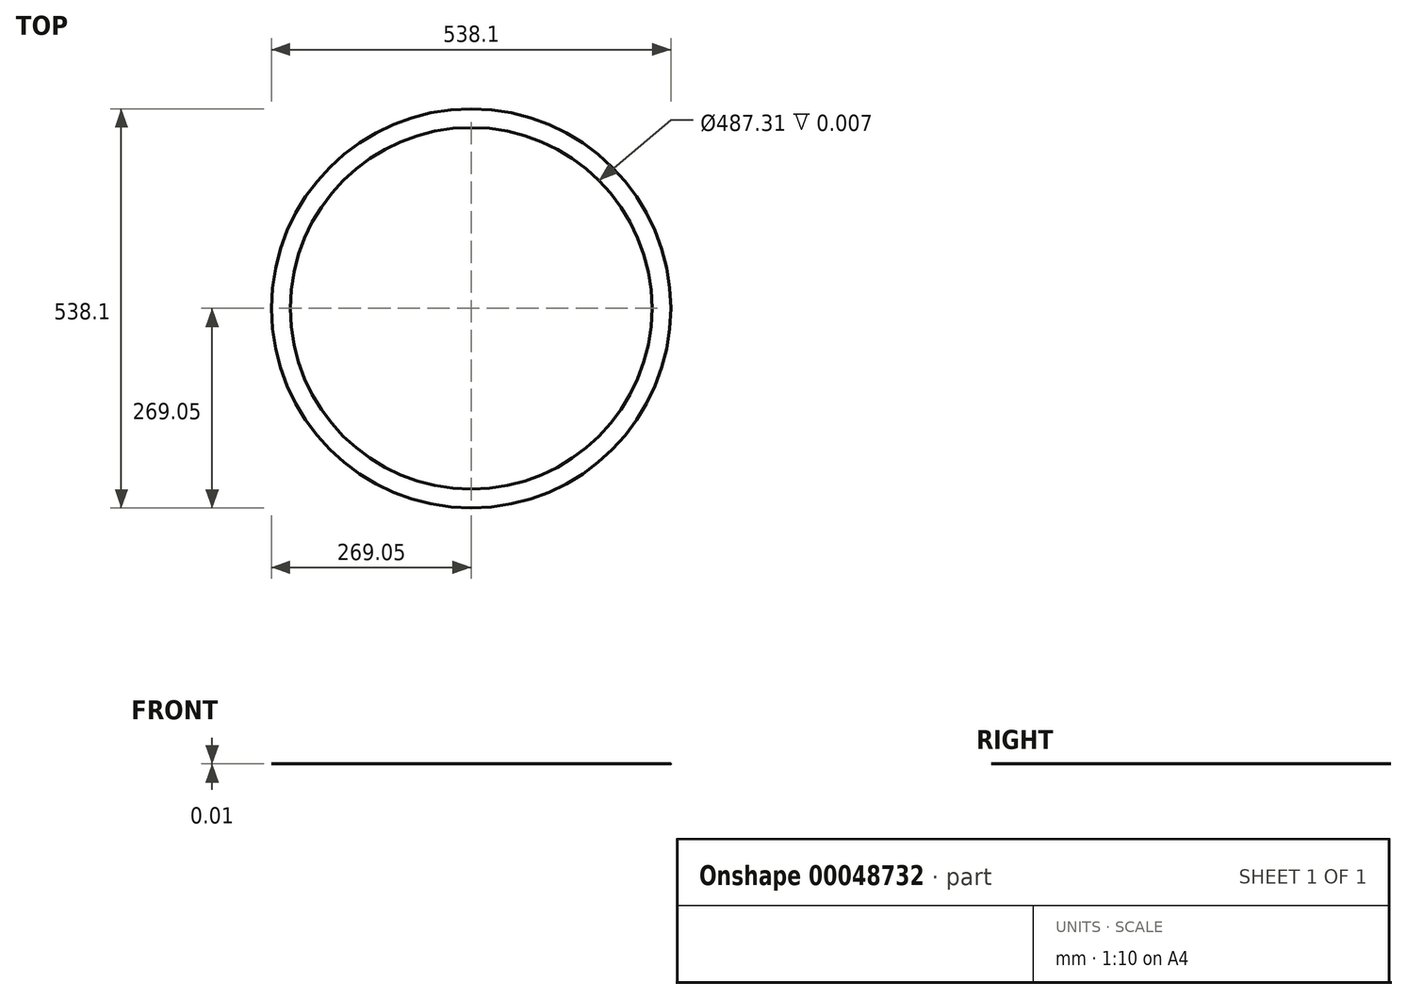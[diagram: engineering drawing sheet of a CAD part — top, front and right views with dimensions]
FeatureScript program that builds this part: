
annotation { "Feature Type Name" : "Feature", "Feature Type Description" : "" }
export const myFeature = defineFeature(function(context is Context, id is Id, definition is map)
    precondition{}
    {
        {
            var Q0;
            Q0=qCreatedBy(makeId("Top.planeOp"),FACE);
            var sketch = newSketch(context, id + "F0", { "sketchPlane" : qUnion([Q0])});
            skCircle(sketch, "E0", {"center": v(0, 0) * mm, "radius": 269.05 * mm});
            skCircle(sketch, "E1", {"center": v(0, 0) * mm, "radius": 243.65 * mm});
            skSolve(sketch);
        }
        {
            var Q0;
            Q0=makeQuery(id+"F0.imprint","IMPRINT",FACE,{"disambiguationData":[TD([[makeQuery(id+"F0.imprint","IMPRINT",EDGE,{"derivedFrom":sQuery(id+"F0.wireOp",EDGE,"E0")}),1.0]])]});
            extrude(context, id + "F1", {"entities" : qUnion([Q0]), "depth" : 3 / 406.4 * mm});
        }
    });
